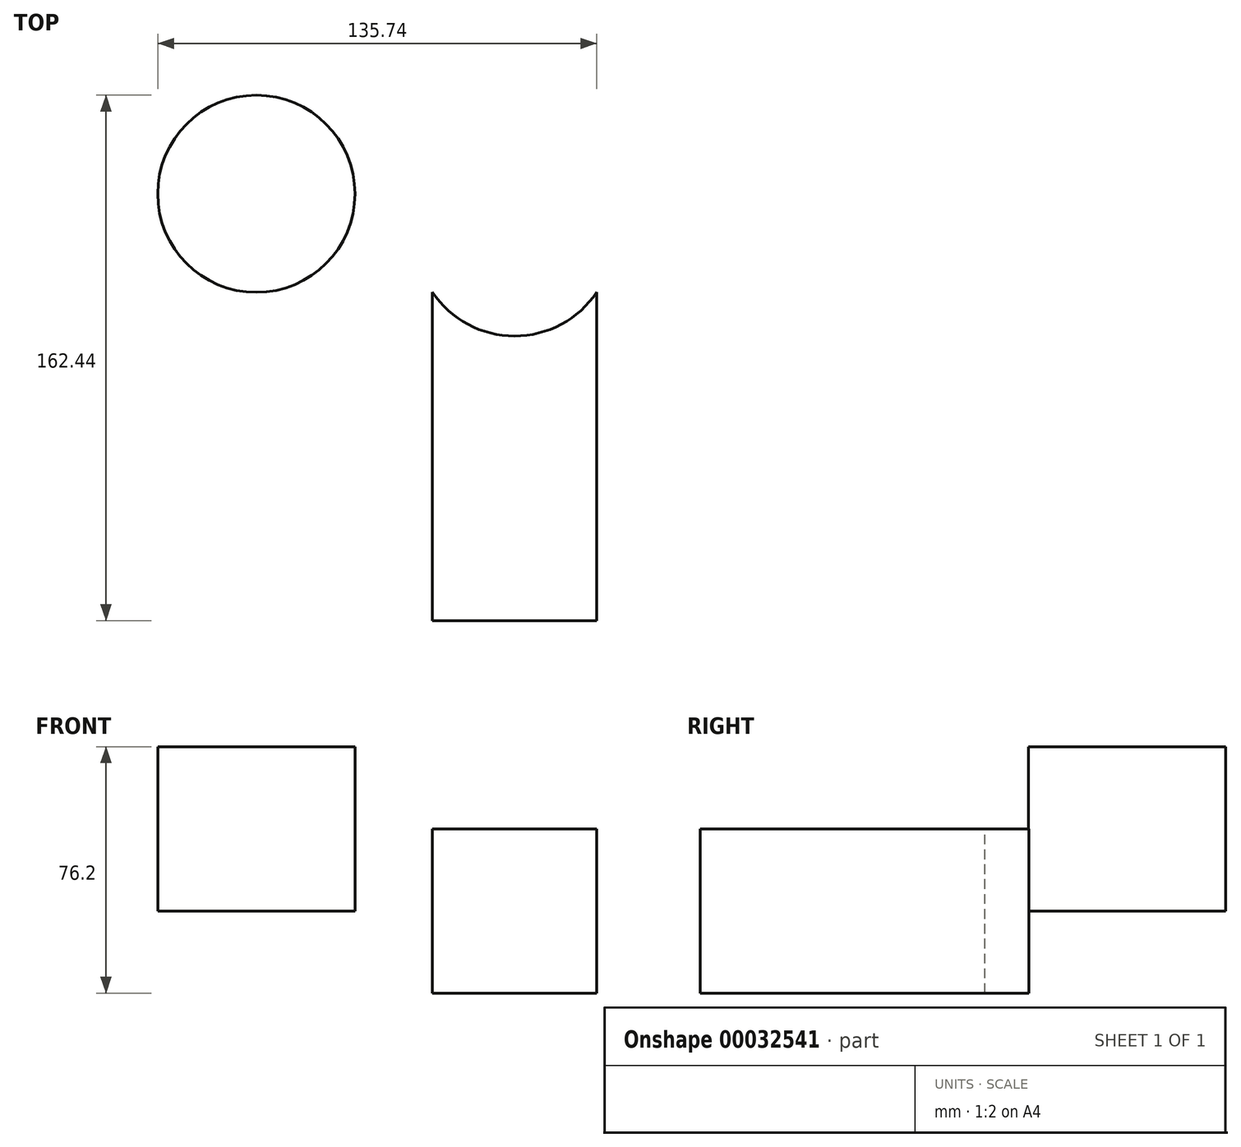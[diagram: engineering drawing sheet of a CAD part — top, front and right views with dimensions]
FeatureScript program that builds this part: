
annotation { "Feature Type Name" : "Feature", "Feature Type Description" : "" }
export const myFeature = defineFeature(function(context is Context, id is Id, definition is map)
    precondition{}
    {
        {
            var Q0;
            Q0=qCreatedBy(makeId("Front.planeOp"),FACE);
            var sketch = newSketch(context, id + "F0", { "sketchPlane" : qUnion([Q0])});
            skLineSegment(sketch, "E0.rect.bottom", {"start": v(-25.4, 25.4) * mm, "end": v(25.4, 25.4) * mm});
            skLineSegment(sketch, "E0.rect.top", {"start": v(-25.4, -25.4) * mm, "end": v(25.4, -25.4) * mm});
            skLineSegment(sketch, "E0.rect.left", {"start": v(-25.4, 25.4) * mm, "end": v(-25.4, -25.4) * mm});
            skLineSegment(sketch, "E0.rect.right", {"start": v(25.4, 25.4) * mm, "end": v(25.4, -25.4) * mm});
            skPoint(sketch, "E0.rect.middle", {"position": v(0, 0) * mm});
            skSolve(sketch);
        }
        {
            var Q0;
            Q0 = qSketchRegion(id + "F0", true);
            extrude(context, id + "F1", {"entities" : qUnion([Q0]), "depth" : 101.6 * mm});
        }
        {
            var Q0;
            Q0=makeQuery(id+"F1.opExtrude","SWEPT_FACE",FACE,{"disambiguationData":[OSD([sQuery(id+"F0.wireOp",EDGE,"E0.rect.bottom")])]});
            var sketch = newSketch(context, id + "F2", { "sketchPlane" : qUnion([Q0])});
            skArc(sketch, "E1", {"start": v(-25.4, 0) * mm, "mid": v(0, -13.63) * mm, "end": v(25.4, 0) * mm});
            skSolve(sketch);
        }
        {
            var Q0;
            Q0 = qSketchRegion(id + "F2", true);
            var Q1;
            Q1=makeQuery(id+"F2.imprint","IMPRINT",FACE,{"disambiguationData":[TD([[makeQuery(id+"F2.imprint","IMPRINT",EDGE,{"derivedFrom":sQuery(id+"F2.wireOp",EDGE,"E1")}),1.0]])]});
            extrude(context, id + "F3", {"entities" : qUnion([Q0, Q1]), "operationType" : NewBodyOperationType.REMOVE, "endBound" : BoundingType.THROUGH_ALL, "oppositeDirection" : true, "depth" : 25.4 * mm});
        }
        {
            var Q0;
            Q0=qCreatedBy(makeId("Top.planeOp"),FACE);
            var sketch = newSketch(context, id + "F4", { "sketchPlane" : qUnion([Q0])});
            skCircle(sketch, "E2", {"center": v(-79.86, 30.36) * mm, "radius": 30.48 * mm});
            skSolve(sketch);
        }
        {
            var Q0;
            Q0=makeQuery(id+"F4.imprint","IMPRINT",FACE,{"disambiguationData":[TD([[makeQuery(id+"F4.imprint","IMPRINT",EDGE,{"derivedFrom":sQuery(id+"F4.wireOp",EDGE,"E2")}),1.0]])]});
            extrude(context, id + "F5", {"entities" : qUnion([Q0]), "depth" : 50.8 * mm});
        }
    });
